# Revit family: Gleiter radial-axial GL-100 m.Lasche, 1xAG
name_source: partatom
category: HLS-Bauteile
revit_build: Autodesk Revit 2017 (Build: 20190507_1515(x64)
units: mm (PartAtom-declared; Revit-internal decimal feet)

## family parameters
Arbeitsebenenbasiert = Ja
Beim Laden mit Abzugskörper schneiden = Nein
Bemaßung runder Anschluss = Durchmesser verwenden
Gemeinsam genutzt = Ja
Immer vertikal = Nein
Raumberechnungspunkt = Nein
Teiletyp = Normal

## types (4) — shared parameters
B = 160 mm  [stored 0.524934 ft]
B1 = 50 mm  [stored 0.164042 ft]
Breite = 186 mm  [stored 0.610236 ft]
DVS = 14 mm  [stored 0.0459318 ft]
Fabrikat = MEFA
Firma = MEFA Befestigungs- und Montagesysteme GmbH
Gleitreibungsfaktor = 0.15 - 0.25
H1 = 7 mm  [stored 0.0229659 ft]
Haftreibungsfaktor = 0,2 - 0,3
Kurztext1 = Gleitelement radial-axial GL 100
L = 125 mm  [stored 0.410105 ft]
L1 = 96 mm  [stored 0.314961 ft]
Länge = 160 mm  [stored 0.524934 ft]
Material Gleitstreifen = Kunststoff
Materialname Gleitstreifen = Polyamid 6
Mengeneinheit = St
Vorgabe-Ansicht = 1219 mm
max. Temperaturbeständigkeit = 100 °C
vpe = 1 St

## per-type parameters (varying)
| type | Artikelnummer | EAN | GL-100, 1xAG | Gewicht | Gewicht pro Bauteil | H | Kurztext2 |
| Gleiter ra-ax GL-100 m.Lasche, 1x M10 | 077048402 | 4250928417770 | Gleiter GL-100, 1xAG : Gleiter GL-100, AG M10 | 1.07 kg | 1.07 kg | 47 mm  [stored 0.154199 ft] | Anschluss 1 x M10 mit Lasche |
| Gleiter ra-ax GL-100 m.Lasche, 1x M12 | 077048302 | 4250928417756 | Gleiter GL-100, 1xAG : Gleiter GL-100, AG M12 | 1.08 kg | 1.08 kg | 49 mm  [stored 0.160761 ft] | Anschluss 1 x M12 mit Lasche |
| Gleiter ra-ax GL-100 m.Lasche, 1x M16 | 077048502 | 4250928417794 | Gleiter GL-100, 1xAG : Gleiter GL-100, AG M16 | 1.09 kg | 1.09 kg | 48 mm  [stored 0.15748 ft] | Anschluss 1 x M16 mit Lasche |
| Gleiter ra-ax GL-100 m.Lasche, 1x 1/2" | 077048602 | 4250928417817 | Gleiter GL-100, 1xAG : Gleiter GL-100, AG Muffe halb Zoll | 1.09 kg | 1.09 kg | 48 mm  [stored 0.15748 ft] | Anschluss 1 x 1/2'' mit Lasche |

note: [stored X ft] marks values corroborated as IEEE doubles in the binary element streams (Revit-internal decimal feet)

## geometry (parser evidence)
native form markers: Sweep x3
no freeform markers — native parametric forms only
